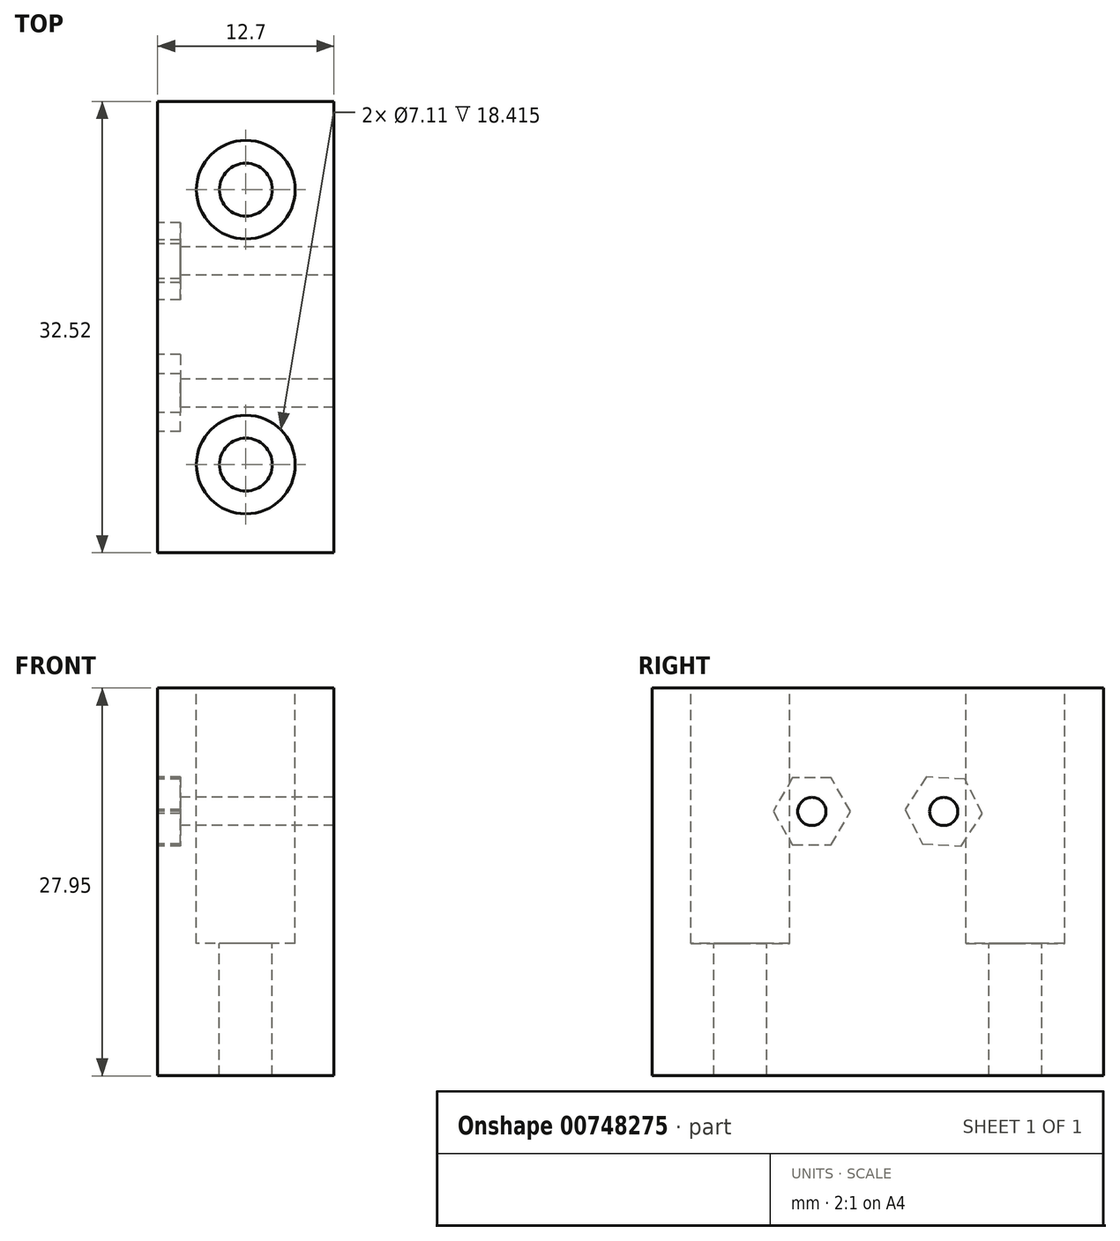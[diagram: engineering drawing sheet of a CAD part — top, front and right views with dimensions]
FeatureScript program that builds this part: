
annotation { "Feature Type Name" : "Feature", "Feature Type Description" : "" }
export const myFeature = defineFeature(function(context is Context, id is Id, definition is map)
    precondition{}
    {
        {
            var Q0;
            Q0=qCreatedBy(makeId("Right.planeOp"),FACE);
            var sketch = newSketch(context, id + "F0", { "sketchPlane" : qUnion([Q0])});
            skLineSegment(sketch, "E0.bottom", {"start": v(9.9, 9.53) * mm, "end": v(-9.9, 9.53) * mm, "construction": true});
            skLineSegment(sketch, "E0.top", {"start": v(9.9, -9.53) * mm, "end": v(-9.9, -9.53) * mm, "construction": true});
            skLineSegment(sketch, "E0.left", {"start": v(9.9, 9.53) * mm, "end": v(9.9, -9.53) * mm, "construction": true});
            skLineSegment(sketch, "E0.right", {"start": v(-9.9, 9.53) * mm, "end": v(-9.9, -9.52) * mm, "construction": true});
            skPoint(sketch, "E0.middle", {"position": v(0, 0) * mm});
            skLineSegment(sketch, "E1", {"start": v(16.26, -9.52) * mm, "end": v(16.26, 18.42) * mm});
            skLineSegment(sketch, "E2", {"start": v(-16.26, -9.53) * mm, "end": v(-16.26, 18.42) * mm});
            skLineSegment(sketch, "E3", {"start": v(-16.26, 18.42) * mm, "end": v(16.26, 18.42) * mm});
            skLineSegment(sketch, "E4", {"start": v(16.26, -9.52) * mm, "end": v(-16.26, -9.52) * mm});
            skSolve(sketch);
        }
        {
            var Q0;
            Q0 = qSketchRegion(id + "F0", true);
            extrude(context, id + "F1", {"entities" : qUnion([Q0]), "depth" : 12.7 * mm, "offsetDistance" : 25.4 * mm});
        }
        {
            var Q0;
            Q0=makeQuery(id+"F1.opExtrude","CAP_FACE",FACE,{"disambiguationData":[OSD([sQuery(id+"F0.wireOp",EDGE,"E1"),sQuery(id+"F0.wireOp",EDGE,"E2"),sQuery(id+"F0.wireOp",EDGE,"E3"),sQuery(id+"F0.wireOp",EDGE,"E4")])],"isStart":true});
            var sketch = newSketch(context, id + "F2", { "sketchPlane" : qUnion([Q0])});
            skLineSegment(sketch, "E5.bottom", {"start": v(4.75, -9.52) * mm, "end": v(-4.75, -9.52) * mm, "construction": true});
            skLineSegment(sketch, "E5.top", {"start": v(4.75, 9.52) * mm, "end": v(-4.75, 9.52) * mm, "construction": true});
            skLineSegment(sketch, "E5.left", {"start": v(4.75, -9.52) * mm, "end": v(4.75, 9.52) * mm, "construction": true});
            skLineSegment(sketch, "E5.right", {"start": v(-4.75, -9.52) * mm, "end": v(-4.75, 9.52) * mm, "construction": true});
            skPoint(sketch, "E5.middle", {"position": v(0, 0) * mm});
            skCircle(sketch, "E6", {"center": v(4.75, 9.52) * mm, "radius": 1.02 * mm});
            skCircle(sketch, "E7", {"center": v(-4.75, 9.52) * mm, "radius": 1.02 * mm});
            skSolve(sketch);
        }
        {
            var Q0;
            Q0 = qSketchRegion(id + "F2", true);
            extrude(context, id + "F3", {"entities" : qUnion([Q0]), "operationType" : NewBodyOperationType.REMOVE, "endBound" : BoundingType.THROUGH_ALL, "oppositeDirection" : true, "depth" : 25.4 * mm, "offsetDistance" : 25.4 * mm});
        }
        {
            var Q0;
            Q0=makeQuery(id+"F1.opExtrude","CAP_FACE",FACE,{"disambiguationData":[OSD([sQuery(id+"F0.wireOp",EDGE,"E1"),sQuery(id+"F0.wireOp",EDGE,"E2"),sQuery(id+"F0.wireOp",EDGE,"E3"),sQuery(id+"F0.wireOp",EDGE,"E4")])],"isStart":true});
            var sketch = newSketch(context, id + "F4", { "sketchPlane" : qUnion([Q0])});
            skCircle(sketch, "E8.cCircle", {"center": v(-4.75, 9.52) * mm, "radius": 2.41 * mm, "construction": true});
            skLineSegment(sketch, "E8.0", {"start": v(-3.5, 12.01) * mm, "end": v(-1.97, 9.68) * mm});
            skLineSegment(sketch, "E8.1", {"start": v(-1.97, 9.68) * mm, "end": v(-3.22, 7.2) * mm});
            skLineSegment(sketch, "E8.2", {"start": v(-3.22, 7.2) * mm, "end": v(-6, 7.04) * mm});
            skLineSegment(sketch, "E8.3", {"start": v(-6, 7.04) * mm, "end": v(-7.53, 9.37) * mm});
            skLineSegment(sketch, "E8.4", {"start": v(-7.53, 9.37) * mm, "end": v(-6.28, 11.86) * mm});
            skLineSegment(sketch, "E8.5", {"start": v(-6.28, 11.86) * mm, "end": v(-3.5, 12.01) * mm});
            skPoint(sketch, "E8.0.midPoint", {"position": v(-2.73, 10.85) * mm});
            skCircle(sketch, "E9.cCircle", {"center": v(4.75, 9.52) * mm, "radius": 2.41 * mm, "construction": true});
            skLineSegment(sketch, "E9.0", {"start": v(3.36, 11.94) * mm, "end": v(6.14, 11.94) * mm});
            skLineSegment(sketch, "E9.1", {"start": v(6.14, 11.94) * mm, "end": v(7.54, 9.52) * mm});
            skLineSegment(sketch, "E9.2", {"start": v(7.54, 9.53) * mm, "end": v(6.14, 7.11) * mm});
            skLineSegment(sketch, "E9.3", {"start": v(6.14, 7.11) * mm, "end": v(3.36, 7.11) * mm});
            skLineSegment(sketch, "E9.4", {"start": v(3.36, 7.11) * mm, "end": v(1.96, 9.52) * mm});
            skLineSegment(sketch, "E9.5", {"start": v(1.96, 9.52) * mm, "end": v(3.36, 11.94) * mm});
            skPoint(sketch, "E9.0.midPoint", {"position": v(4.75, 11.94) * mm});
            skSolve(sketch);
        }
        {
            var Q0;
            Q0 = qSketchRegion(id + "F4", true);
            extrude(context, id + "F5", {"entities" : qUnion([Q0]), "operationType" : NewBodyOperationType.REMOVE, "oppositeDirection" : true, "depth" : 1.65 * mm, "offsetDistance" : 25.4 * mm});
        }
        {
            var Q0;
            Q0=makeQuery(id+"F1.opExtrude","SWEPT_FACE",FACE,{"disambiguationData":[OSD([sQuery(id+"F0.wireOp",EDGE,"E3")])]});
            var sketch = newSketch(context, id + "F6", { "sketchPlane" : qUnion([Q0])});
            skLineSegment(sketch, "E10", {"start": v(6.35, 16.26) * mm, "end": v(6.35, -16.26) * mm, "construction": true});
            skLineSegment(sketch, "E11", {"start": v(0, 9.9) * mm, "end": v(12.7, 9.9) * mm, "construction": true});
            skLineSegment(sketch, "E12", {"start": v(0, -9.9) * mm, "end": v(12.7, -9.9) * mm, "construction": true});
            skCircle(sketch, "E13", {"center": v(6.35, -9.9) * mm, "radius": 1.9 * mm});
            skCircle(sketch, "E14", {"center": v(6.35, 9.9) * mm, "radius": 1.9 * mm});
            skSolve(sketch);
        }
        {
            var Q0;
            Q0 = qSketchRegion(id + "F6", true);
            extrude(context, id + "F7", {"entities" : qUnion([Q0]), "operationType" : NewBodyOperationType.REMOVE, "endBound" : BoundingType.THROUGH_ALL, "oppositeDirection" : true, "depth" : 25.4 * mm, "offsetDistance" : 25.4 * mm});
        }
        {
            var Q0;
            Q0=makeQuery(id+"F1.opExtrude","SWEPT_FACE",FACE,{"disambiguationData":[OSD([sQuery(id+"F0.wireOp",EDGE,"E3")])]});
            var sketch = newSketch(context, id + "F8", { "sketchPlane" : qUnion([Q0])});
            skCircle(sketch, "E15", {"center": v(6.35, 9.9) * mm, "radius": 3.56 * mm});
            skCircle(sketch, "E16", {"center": v(6.35, -9.9) * mm, "radius": 3.56 * mm});
            skSolve(sketch);
        }
        {
            var Q0;
            Q0 = qSketchRegion(id + "F8", true);
            extrude(context, id + "F9", {"entities" : qUnion([Q0]), "operationType" : NewBodyOperationType.REMOVE, "oppositeDirection" : true, "depth" : 18.42 * mm, "offsetDistance" : 25.4 * mm});
        }
    });
